# Revit family: Gira_289800
name_source: partatom
category: Electrical Fixtures
revit_build: Autodesk Revit 2017 (Build: 20160225_1515(x64)
units: mm (PartAtom-declared; Revit-internal decimal feet)

## family parameters
Cut with Voids When Loaded = No
Host = Face
Maintain Annotation Orientation = No
Part Type = Normal
Room Calculation Point = No
Round Connector Dimension = Use Diameter
Shared = No

## types (1)
- DB 3-g flat Gira E22
    Available = No
    BIM (1) = https://media.stage.bim.site
    Category = Box/housing for built-in mounting in the wall/ceiling
    Construction type = Built-in installation box (device box)
    Data sheet (1) = https://katalog.gira.de
    Default Elevation = 1219 mm
    Description = DB 3g flat E22,Gira E2, Gira E22 device box for flat installation,,3-gang,Features:,- With the aid of the Gira device box and cover frame for flat installation, the Gira E2 and Gira E22 design lines can be installed flat on the wall.,- For flush-mounted installation in brickwork, the device box is inserted into an flush-mounted installation box, which is then placed in the wall.,,Notes :,- The device box has no cable retainer.
    Equipped with = None
    GTIN = 4010337066538
    HAN = 289800
    HeinzeBIM = https://bimportal.heinze.de
    Manufacturer = Gira
    Manufacturer URL = https://www.gira.de
    Model = Other
    Mounting switching equipment = Screwing
    Name = DB 3-g flat Gira E22
    Shape = Square
    URL = http://katalog.gira.de

## geometry (parser evidence)
native form markers: Blend x2, Sweep x2
no freeform markers — native parametric forms only
